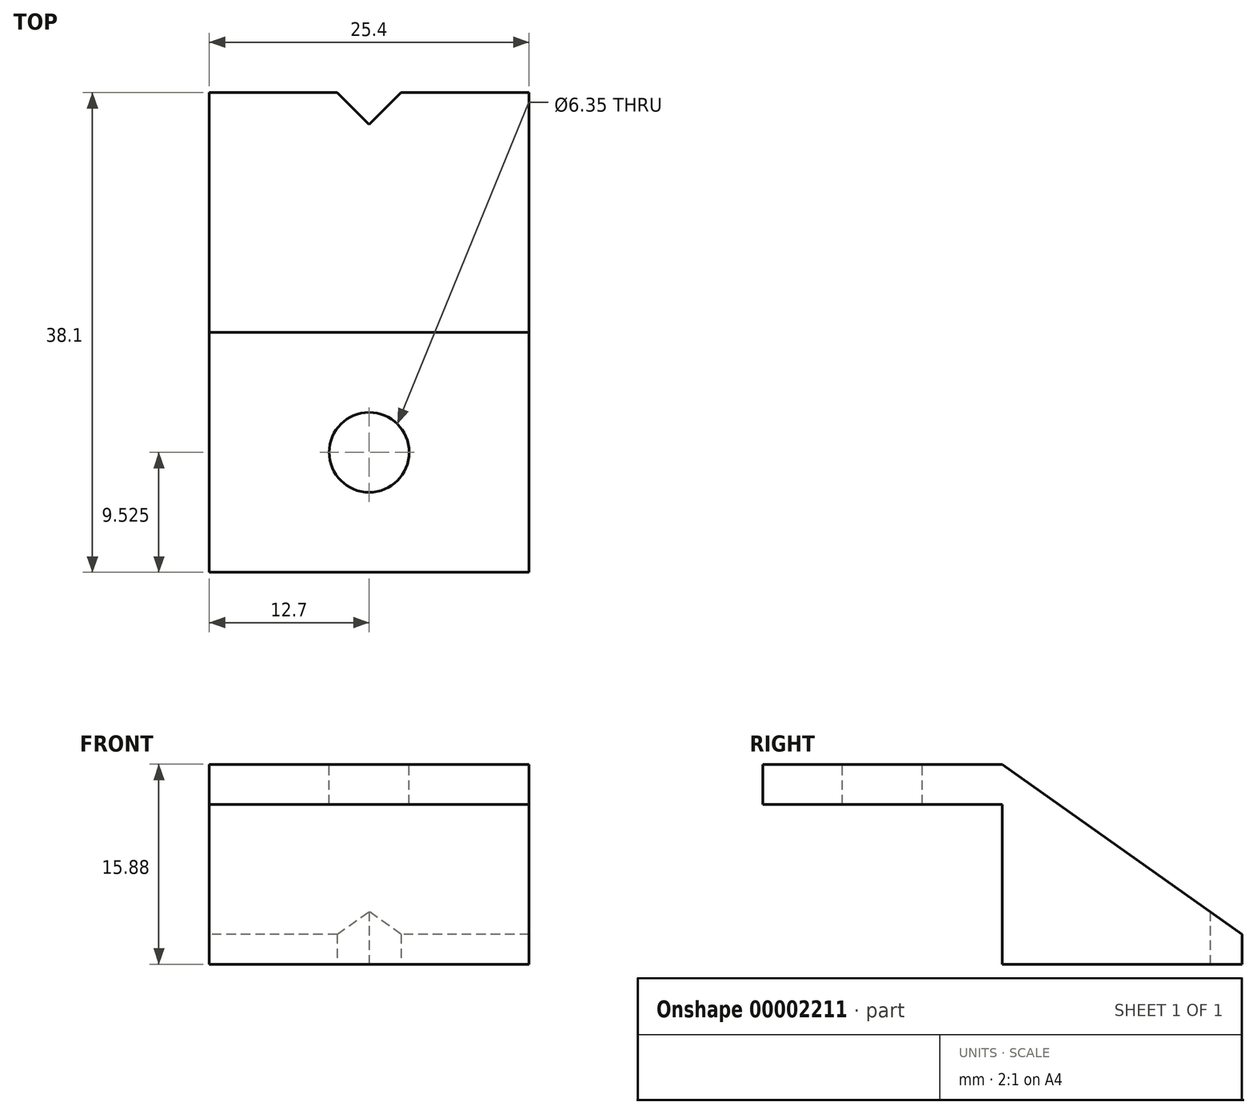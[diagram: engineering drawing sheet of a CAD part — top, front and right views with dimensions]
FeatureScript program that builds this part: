
annotation { "Feature Type Name" : "Feature", "Feature Type Description" : "" }
export const myFeature = defineFeature(function(context is Context, id is Id, definition is map)
    precondition{}
    {
        {
            var Q0;
            Q0=qCreatedBy(makeId("Right.planeOp"),FACE);
            var sketch = newSketch(context, id + "F0", { "sketchPlane" : qUnion([Q0])});
            skLineSegment(sketch, "E0", {"start": v(0, 0) * mm, "end": v(19.05, 0) * mm});
            skLineSegment(sketch, "E1", {"start": v(19.05, 0) * mm, "end": v(19.05, 2.38) * mm});
            skLineSegment(sketch, "E2", {"start": v(19.05, 2.38) * mm, "end": v(0, 15.88) * mm});
            skLineSegment(sketch, "E3", {"start": v(0, 15.87) * mm, "end": v(-19.05, 15.87) * mm});
            skLineSegment(sketch, "E4", {"start": v(-19.05, 15.88) * mm, "end": v(-19.05, 12.7) * mm});
            skLineSegment(sketch, "E5", {"start": v(-19.05, 12.7) * mm, "end": v(0, 12.7) * mm});
            skLineSegment(sketch, "E6", {"start": v(0, 12.7) * mm, "end": v(0, 0) * mm});
            skSolve(sketch);
        }
        {
            var Q0;
            Q0=makeQuery(id+"F0.imprint","IMPRINT",FACE,{"disambiguationData":[TD([[makeQuery(id+"F0.imprint","IMPRINT",EDGE,{"derivedFrom":sQuery(id+"F0.wireOp",EDGE,"E0")}),1.0]])]});
            extrude(context, id + "F1", {"entities" : qUnion([Q0]), "depth" : 25.4 * mm});
        }
        {
            var Q0;
            Q0=makeQuery(id+"F1.opExtrude","SWEPT_FACE",FACE,{"disambiguationData":[OSD([sQuery(id+"F0.wireOp",EDGE,"E3")])]});
            var sketch = newSketch(context, id + "F2", { "sketchPlane" : qUnion([Q0])});
            skLineSegment(sketch, "E7", {"start": v(0, -9.52) * mm, "end": v(25.4, -9.52) * mm, "construction": true});
            skLineSegment(sketch, "E8", {"start": v(12.7, -19.05) * mm, "end": v(12.7, 0) * mm, "construction": true});
            skCircle(sketch, "E9", {"center": v(12.7, -9.52) * mm, "radius": 3.18 * mm});
            skSolve(sketch);
        }
        {
            var Q0;
            Q0=makeQuery(id+"F2.imprint","IMPRINT",FACE,{"disambiguationData":[TD([[makeQuery(id+"F2.imprint","IMPRINT",EDGE,{"derivedFrom":sQuery(id+"F2.wireOp",EDGE,"E9")}),1.0]])]});
            extrude(context, id + "F3", {"entities" : qUnion([Q0]), "operationType" : NewBodyOperationType.REMOVE, "endBound" : BoundingType.THROUGH_ALL, "oppositeDirection" : true, "depth" : 25.4 * mm});
        }
        {
            var Q0;
            Q0=makeQuery(id+"F1.opExtrude","SWEPT_FACE",FACE,{"disambiguationData":[OSD([sQuery(id+"F0.wireOp",EDGE,"E0")])]});
            var sketch = newSketch(context, id + "F4", { "sketchPlane" : qUnion([Q0])});
            skLineSegment(sketch, "E10", {"start": v(12.7, 0) * mm, "end": v(12.7, -19.05) * mm, "construction": true});
            skLineSegment(sketch, "E11", {"start": v(15.24, -19.05) * mm, "end": v(12.7, -16.51) * mm});
            skLineSegment(sketch, "E12.0.MirrorCS", {"start": v(10.16, -19.05) * mm, "end": v(12.7, -16.51) * mm});
            skLineSegment(sketch, "E13", {"start": v(10.16, -19.05) * mm, "end": v(15.24, -19.05) * mm});
            skSolve(sketch);
        }
        {
            var Q0;
            Q0=makeQuery(id+"F4.imprint","IMPRINT",FACE,{"disambiguationData":[TD([[makeQuery(id+"F4.imprint","IMPRINT",EDGE,{"derivedFrom":sQuery(id+"F4.wireOp",EDGE,"E11")}),1.0]])]});
            extrude(context, id + "F5", {"entities" : qUnion([Q0]), "operationType" : NewBodyOperationType.REMOVE, "endBound" : BoundingType.THROUGH_ALL, "oppositeDirection" : true, "depth" : 25.4 * mm});
        }
    });
